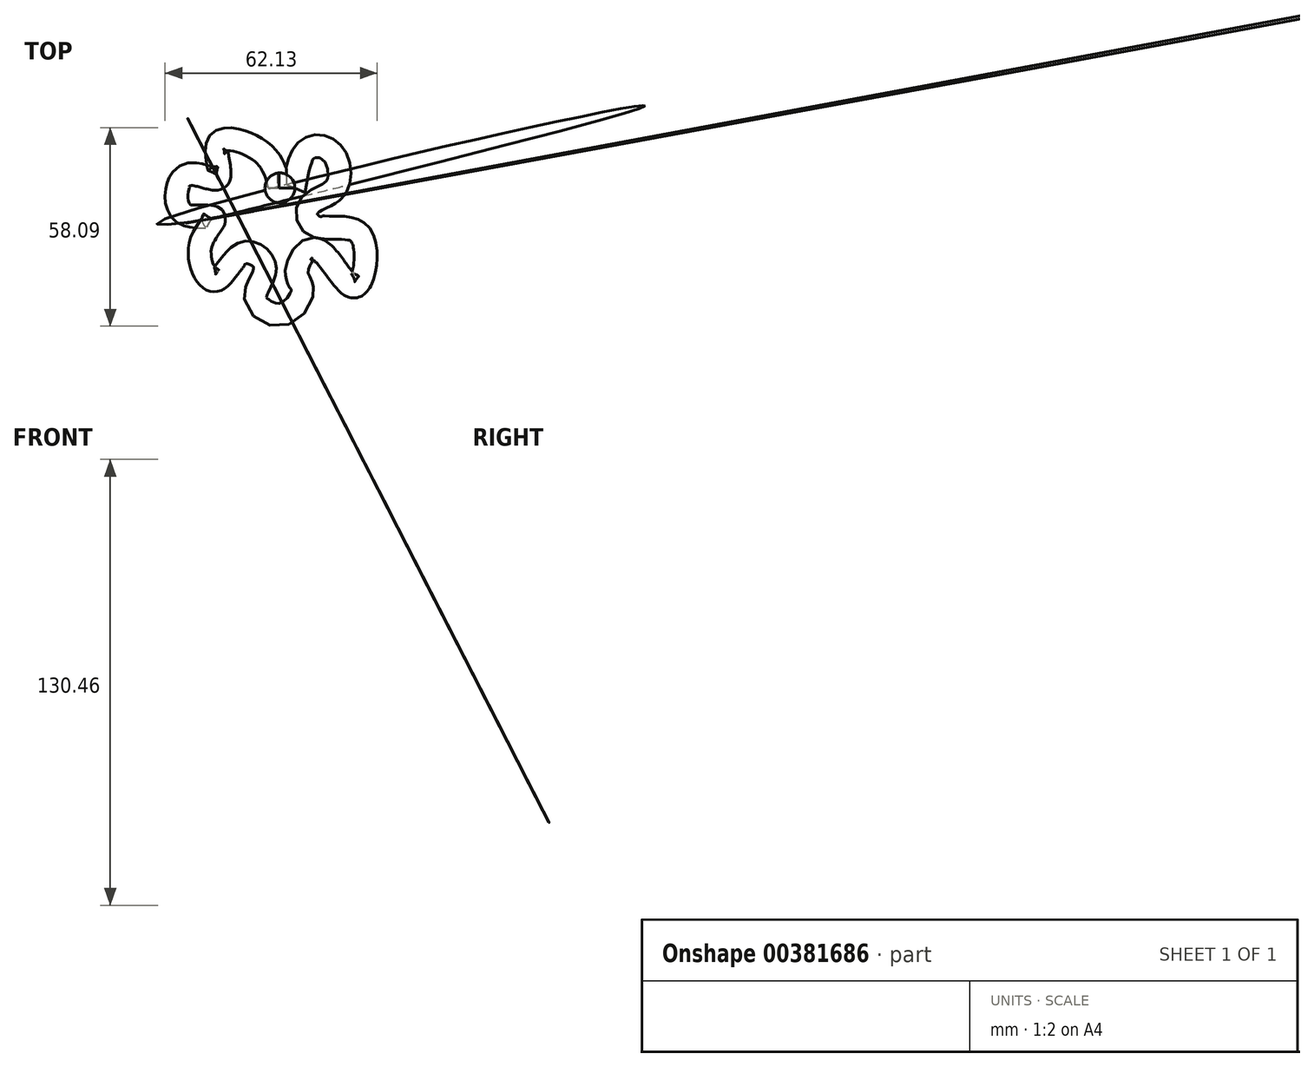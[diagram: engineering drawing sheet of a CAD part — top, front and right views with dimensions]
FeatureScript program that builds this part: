
annotation { "Feature Type Name" : "Feature", "Feature Type Description" : "" }
export const myFeature = defineFeature(function(context is Context, id is Id, definition is map)
    precondition{}
    {
        {
            var Q0;
            Q0=qCreatedBy(makeId("Front.planeOp"),FACE);
            var sketch = newSketch(context, id + "F0", { "sketchPlane" : qUnion([Q0])});
            skCircle(sketch, "E0", {"center": v(0, 0) * mm, "radius": 3.46 * mm});
            skSolve(sketch);
        }
        {
            var Q0;
            Q0=qCreatedBy(makeId("Top.planeOp"),FACE);
            var sketch = newSketch(context, id + "F1", { "sketchPlane" : qUnion([Q0])});
            skFitSpline(sketch, "E1", {"points": [v(0, 0) * mm, v(-5.55, 10.58) * mm, v(-17.97, 12.94) * mm, v(-18.07, 2.99) * mm, v(-27.25, 3.66) * mm, v(-28.6, -6.99) * mm, v(-19.45, -8.79) * mm, v(-23.26, -16.97) * mm, v(-19.05, -26.98) * mm, v(-10.65, -19.13) * mm, v(-4.49, -23.36) * mm, v(-7.09, -31.98) * mm, v(0, -37.03) * mm, v(6.47, -30.46) * mm, v(4.96, -24.3) * mm, v(10.69, -18.04) * mm, v(21.82, -28.78) * mm, v(23.57, -13.9) * mm, v(10.14, -10.92) * mm, v(8.72, -5.23) * mm, v(16.27, 0) * mm, v(15.36, 10.17) * mm, v(8.36, 11.37) * mm, v(4.15, 0) * mm], "startDerivative": vector(-56.53, 241.26) * mm, "endDerivative": vector(-49.68, -300.8) * mm});
            skSolve(sketch);
        }
        {
            var Q0;
            Q0=makeQuery(id+"F0.imprint","IMPRINT",FACE,{"disambiguationData":[TD([[makeQuery(id+"F0.imprint","IMPRINT",EDGE,{"derivedFrom":sQuery(id+"F0.wireOp",EDGE,"E0")}),1.0]])]});
            var Q1;
            Q1=sQuery(id+"F1.wireOp",EDGE,"E1");
            sweep(context, id + "F2", {"profiles" : qUnion([Q0]), "path" : qUnion([Q1])});
        }
        {
            var Q0;
            Q0=qCreatedBy(makeId("Top.planeOp"),FACE);
            var sketch = newSketch(context, id + "F3", { "sketchPlane" : qUnion([Q0])});
            skCircle(sketch, "E2", {"center": v(0, 0) * mm, "radius": 4.38 * mm});
            skSolve(sketch);
        }
        {
            var Q0;
            Q0=makeQuery(id+"F3.imprint","IMPRINT",FACE,{"disambiguationData":[TD([[makeQuery(id+"F3.imprint","IMPRINT",EDGE,{"derivedFrom":sQuery(id+"F3.wireOp",EDGE,"E2")}),1.0]])]});
            extrude(context, id + "F4", {"entities" : qUnion([Q0]), "operationType" : NewBodyOperationType.ADD, "depth" : 127 * mm});
        }
        {
            var Q0;
            Q0=qCreatedBy(makeId("Front.planeOp"),FACE);
            var sketch = newSketch(context, id + "F5", { "sketchPlane" : qUnion([Q0])});
            skFitSpline(sketch, "E3", {"points": [v(0, 130.83) * mm, v(0, 72.8) * mm, v(3.2, 58.96) * mm, v(10.13, 44.46) * mm, v(21, 26.66) * mm, v(44.74, 35.23) * mm, v(51.67, 66.54) * mm, v(39.47, 99.5) * mm, v(6.5, 148.63) * mm, v(-3.72, 152.25) * mm, v(-2.73, 145) * mm, v(0, 140.39) * mm, v(0, 130.83) * mm]});
            skSolve(sketch);
        }
        {
            var Q0;
            Q0=makeQuery(id+"F5.imprint","IMPRINT",FACE,{"disambiguationData":[TD([[makeQuery(id+"F5.imprint","IMPRINT",EDGE,{"derivedFrom":sQuery(id+"F5.wireOp",EDGE,"E3")}),1.0]])]});
            extrude(context, id + "F6", {"entities" : qUnion([Q0]), "operationType" : NewBodyOperationType.REMOVE, "endBound" : BoundingType.THROUGH_ALL, "oppositeDirection" : true, "depth" : 25.4 * mm});
        }
    });
